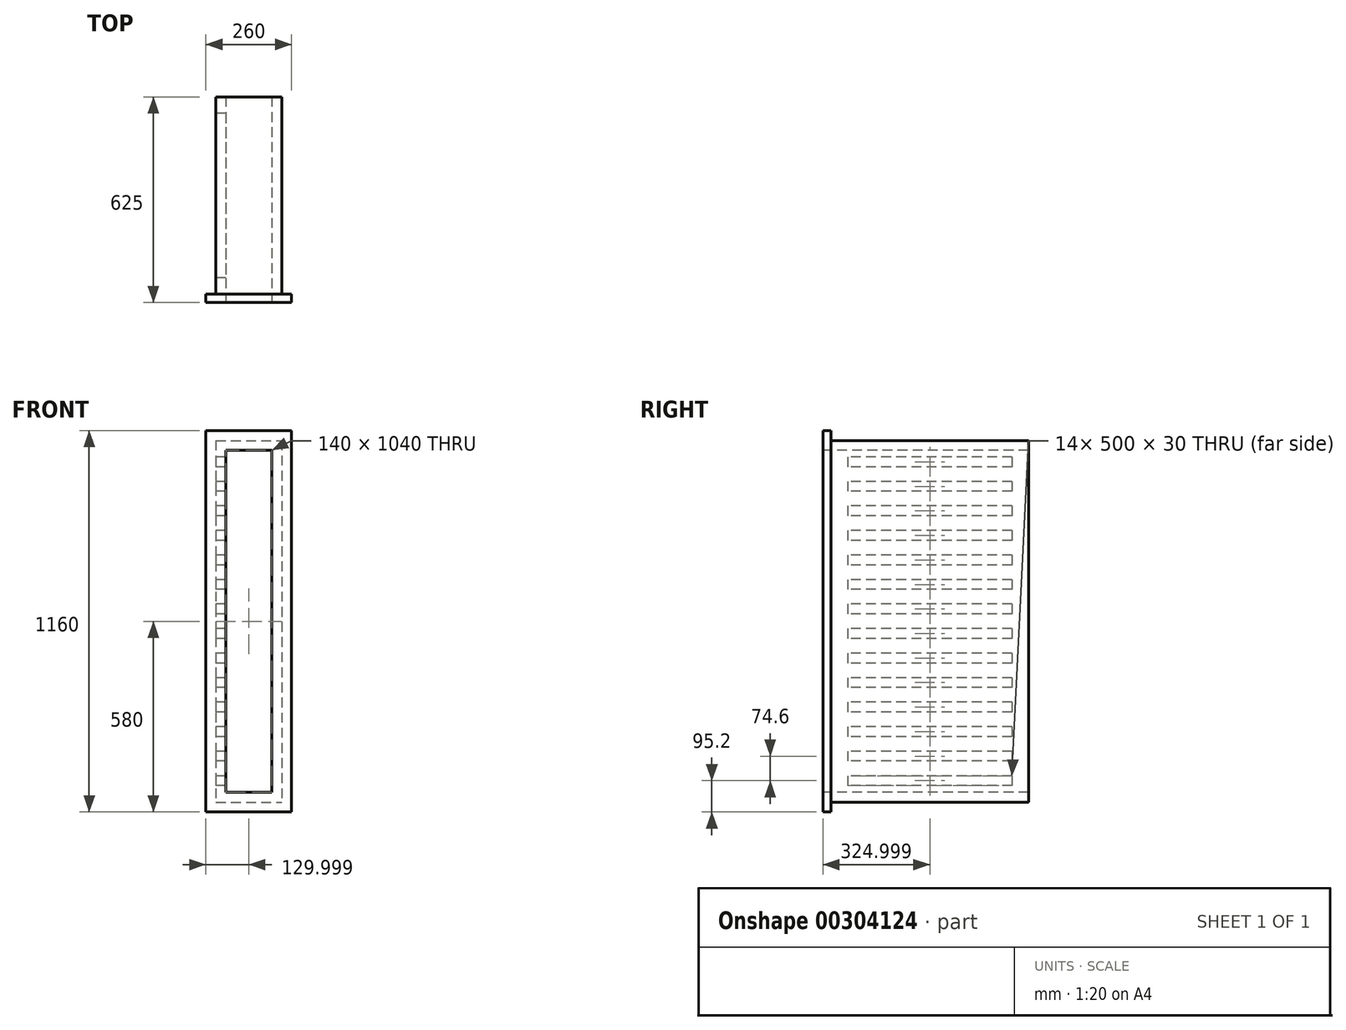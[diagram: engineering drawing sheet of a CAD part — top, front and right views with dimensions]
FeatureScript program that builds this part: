
annotation { "Feature Type Name" : "Feature", "Feature Type Description" : "" }
export const myFeature = defineFeature(function(context is Context, id is Id, definition is map)
    precondition{}
    {
        {
            var Q0;
            Q0=qCreatedBy(makeId("Top.planeOp"),FACE);
            var sketch = newSketch(context, id + "F0", { "sketchPlane" : qUnion([Q0])});
            skLineSegment(sketch, "E0.bottom", {"start": v(-110.21, 294.83) * mm, "end": v(89.79, 294.83) * mm});
            skLineSegment(sketch, "E0.top", {"start": v(-110.21, -305.17) * mm, "end": v(89.79, -305.17) * mm});
            skLineSegment(sketch, "E0.left", {"start": v(-110.21, 294.83) * mm, "end": v(-110.21, -305.17) * mm});
            skLineSegment(sketch, "E0.right", {"start": v(89.79, 294.83) * mm, "end": v(89.79, -305.17) * mm});
            skSolve(sketch);
        }
        {
            var Q0;
            Q0=makeQuery(id+"F0.imprint","IMPRINT",FACE,{"disambiguationData":[TD([[makeQuery(id+"F0.imprint","IMPRINT",EDGE,{"derivedFrom":sQuery(id+"F0.wireOp",EDGE,"E0.bottom")}),-1.0]])]});
            extrude(context, id + "F1", {"entities" : qUnion([Q0]), "depth" : 1100 * mm, "offsetDistance" : 25 * mm});
        }
        {
            var Q0;
            Q0=makeQuery(id+"F1.opExtrude","SWEPT_FACE",FACE,{"disambiguationData":[OSD([sQuery(id+"F0.wireOp",EDGE,"E0.top")])]});
            var sketch = newSketch(context, id + "F2", { "sketchPlane" : qUnion([Q0])});
            skLineSegment(sketch, "E1.bottom", {"start": v(59.79, 1070) * mm, "end": v(-80.21, 1070) * mm});
            skLineSegment(sketch, "E1.top", {"start": v(59.79, 30) * mm, "end": v(-80.21, 30) * mm});
            skLineSegment(sketch, "E1.left", {"start": v(59.79, 1070) * mm, "end": v(59.79, 30) * mm});
            skLineSegment(sketch, "E1.right", {"start": v(-80.21, 1070) * mm, "end": v(-80.21, 30) * mm});
            skSolve(sketch);
        }
        {
            var Q0;
            Q0=makeQuery(id+"F2.imprint","IMPRINT",FACE,{"disambiguationData":[TD([[makeQuery(id+"F2.imprint","IMPRINT",EDGE,{"derivedFrom":sQuery(id+"F2.wireOp",EDGE,"E1.bottom")}),1.0]])]});
            extrude(context, id + "F3", {"entities" : qUnion([Q0]), "operationType" : NewBodyOperationType.REMOVE, "endBound" : BoundingType.UP_TO_NEXT, "oppositeDirection" : true, "depth" : 25 * mm, "offsetDistance" : 25 * mm});
        }
        {
            var Q0;
            Q0=makeQuery(id+"F1.opExtrude","SWEPT_FACE",FACE,{"disambiguationData":[OSD([sQuery(id+"F0.wireOp",EDGE,"E0.left")])]});
            var sketch = newSketch(context, id + "F4", { "sketchPlane" : qUnion([Q0])});
            skLineSegment(sketch, "E2.bottom", {"start": v(-244.83, 1050) * mm, "end": v(255.17, 1050) * mm});
            skLineSegment(sketch, "E2.top", {"start": v(-244.83, 1020) * mm, "end": v(255.17, 1020) * mm});
            skLineSegment(sketch, "E2.left", {"start": v(-244.83, 1050) * mm, "end": v(-244.83, 1020) * mm});
            skLineSegment(sketch, "E2.right", {"start": v(255.17, 1050) * mm, "end": v(255.17, 1020) * mm});
            skLineSegment(sketch, "E3.bottom", {"start": v(-244.83, 900.8) * mm, "end": v(255.17, 900.8) * mm});
            skLineSegment(sketch, "E3.top", {"start": v(-244.83, 870.8) * mm, "end": v(255.17, 870.8) * mm});
            skLineSegment(sketch, "E3.left", {"start": v(-244.83, 900.8) * mm, "end": v(-244.83, 870.8) * mm});
            skLineSegment(sketch, "E3.right", {"start": v(255.17, 900.8) * mm, "end": v(255.17, 870.8) * mm});
            skLineSegment(sketch, "E4.bottom", {"start": v(-244.83, 751.6) * mm, "end": v(255.17, 751.6) * mm});
            skLineSegment(sketch, "E4.top", {"start": v(-244.83, 721.6) * mm, "end": v(255.17, 721.6) * mm});
            skLineSegment(sketch, "E4.left", {"start": v(-244.83, 751.6) * mm, "end": v(-244.83, 721.6) * mm});
            skLineSegment(sketch, "E4.right", {"start": v(255.17, 751.6) * mm, "end": v(255.17, 721.6) * mm});
            skLineSegment(sketch, "E5.bottom", {"start": v(-244.83, 677) * mm, "end": v(255.17, 677) * mm});
            skLineSegment(sketch, "E5.top", {"start": v(-244.83, 647) * mm, "end": v(255.17, 647) * mm});
            skLineSegment(sketch, "E5.left", {"start": v(-244.83, 677) * mm, "end": v(-244.83, 647) * mm});
            skLineSegment(sketch, "E5.right", {"start": v(255.17, 677) * mm, "end": v(255.17, 647) * mm});
            skLineSegment(sketch, "E6.bottom", {"start": v(-244.83, 602.4) * mm, "end": v(255.17, 602.4) * mm});
            skLineSegment(sketch, "E6.top", {"start": v(-244.83, 572.4) * mm, "end": v(255.17, 572.4) * mm});
            skLineSegment(sketch, "E6.left", {"start": v(-244.83, 602.4) * mm, "end": v(-244.83, 572.4) * mm});
            skLineSegment(sketch, "E6.right", {"start": v(255.17, 602.4) * mm, "end": v(255.17, 572.4) * mm});
            skLineSegment(sketch, "E7.bottom", {"start": v(-244.83, 527.8) * mm, "end": v(255.17, 527.8) * mm});
            skLineSegment(sketch, "E7.top", {"start": v(-244.83, 497.8) * mm, "end": v(255.17, 497.8) * mm});
            skLineSegment(sketch, "E7.left", {"start": v(-244.83, 527.8) * mm, "end": v(-244.83, 497.8) * mm});
            skLineSegment(sketch, "E7.right", {"start": v(255.17, 527.8) * mm, "end": v(255.17, 497.8) * mm});
            skLineSegment(sketch, "E8.bottom", {"start": v(-244.83, 453.2) * mm, "end": v(255.17, 453.2) * mm});
            skLineSegment(sketch, "E8.top", {"start": v(-244.83, 423.2) * mm, "end": v(255.17, 423.2) * mm});
            skLineSegment(sketch, "E8.left", {"start": v(-244.83, 453.2) * mm, "end": v(-244.83, 423.2) * mm});
            skLineSegment(sketch, "E8.right", {"start": v(255.17, 453.2) * mm, "end": v(255.17, 423.2) * mm});
            skLineSegment(sketch, "E9.bottom", {"start": v(-244.83, 378.6) * mm, "end": v(255.17, 378.6) * mm});
            skLineSegment(sketch, "E9.top", {"start": v(-244.83, 348.6) * mm, "end": v(255.17, 348.6) * mm});
            skLineSegment(sketch, "E9.left", {"start": v(-244.83, 378.6) * mm, "end": v(-244.83, 348.6) * mm});
            skLineSegment(sketch, "E9.right", {"start": v(255.17, 378.6) * mm, "end": v(255.17, 348.6) * mm});
            skLineSegment(sketch, "E10.bottom", {"start": v(-244.83, 304) * mm, "end": v(255.17, 304) * mm});
            skLineSegment(sketch, "E10.top", {"start": v(-244.83, 274) * mm, "end": v(255.17, 274) * mm});
            skLineSegment(sketch, "E10.left", {"start": v(-244.83, 304) * mm, "end": v(-244.83, 274) * mm});
            skLineSegment(sketch, "E10.right", {"start": v(255.17, 304) * mm, "end": v(255.17, 274) * mm});
            skLineSegment(sketch, "E11.bottom", {"start": v(-244.83, 229.4) * mm, "end": v(255.17, 229.4) * mm});
            skLineSegment(sketch, "E11.top", {"start": v(-244.83, 199.4) * mm, "end": v(255.17, 199.4) * mm});
            skLineSegment(sketch, "E11.left", {"start": v(-244.83, 229.4) * mm, "end": v(-244.83, 199.4) * mm});
            skLineSegment(sketch, "E11.right", {"start": v(255.17, 229.4) * mm, "end": v(255.17, 199.4) * mm});
            skLineSegment(sketch, "E12.bottom", {"start": v(-244.83, 154.8) * mm, "end": v(255.17, 154.8) * mm});
            skLineSegment(sketch, "E12.top", {"start": v(-244.83, 124.8) * mm, "end": v(255.17, 124.8) * mm});
            skLineSegment(sketch, "E12.left", {"start": v(-244.83, 154.8) * mm, "end": v(-244.83, 124.8) * mm});
            skLineSegment(sketch, "E12.right", {"start": v(255.17, 154.8) * mm, "end": v(255.17, 124.8) * mm});
            skLineSegment(sketch, "E13.bottom", {"start": v(-244.83, 80.2) * mm, "end": v(255.17, 80.2) * mm});
            skLineSegment(sketch, "E13.top", {"start": v(-244.83, 50.2) * mm, "end": v(255.17, 50.2) * mm});
            skLineSegment(sketch, "E13.left", {"start": v(-244.83, 80.2) * mm, "end": v(-244.83, 50.2) * mm});
            skLineSegment(sketch, "E13.right", {"start": v(255.17, 80.2) * mm, "end": v(255.17, 50.2) * mm});
            skLineSegment(sketch, "E14.bottom", {"start": v(-244.83, 826.2) * mm, "end": v(255.17, 826.2) * mm});
            skLineSegment(sketch, "E14.top", {"start": v(-244.83, 796.2) * mm, "end": v(255.17, 796.2) * mm});
            skLineSegment(sketch, "E14.left", {"start": v(-244.83, 826.2) * mm, "end": v(-244.83, 796.2) * mm});
            skLineSegment(sketch, "E14.right", {"start": v(255.17, 826.2) * mm, "end": v(255.17, 796.2) * mm});
            skLineSegment(sketch, "E15.bottom", {"start": v(-244.83, 975.4) * mm, "end": v(255.17, 975.4) * mm});
            skLineSegment(sketch, "E15.top", {"start": v(-244.83, 945.4) * mm, "end": v(255.17, 945.4) * mm});
            skLineSegment(sketch, "E15.left", {"start": v(-244.83, 975.4) * mm, "end": v(-244.83, 945.4) * mm});
            skLineSegment(sketch, "E15.right", {"start": v(255.17, 975.4) * mm, "end": v(255.17, 945.4) * mm});
            skSolve(sketch);
        }
        {
            var Q0;
            Q0=makeQuery(id+"F4.imprint","IMPRINT",FACE,{"disambiguationData":[TD([[makeQuery(id+"F4.imprint","IMPRINT",EDGE,{"derivedFrom":sQuery(id+"F4.wireOp",EDGE,"E2.bottom")}),-1.0]])]});
            var Q1;
            Q1=makeQuery(id+"F4.imprint","IMPRINT",FACE,{"disambiguationData":[TD([[makeQuery(id+"F4.imprint","IMPRINT",EDGE,{"derivedFrom":sQuery(id+"F4.wireOp",EDGE,"E15.bottom")}),-1.0]])]});
            var Q2;
            Q2=makeQuery(id+"F4.imprint","IMPRINT",FACE,{"disambiguationData":[TD([[makeQuery(id+"F4.imprint","IMPRINT",EDGE,{"derivedFrom":sQuery(id+"F4.wireOp",EDGE,"E3.bottom")}),-1.0]])]});
            var Q3;
            Q3=makeQuery(id+"F4.imprint","IMPRINT",FACE,{"disambiguationData":[TD([[makeQuery(id+"F4.imprint","IMPRINT",EDGE,{"derivedFrom":sQuery(id+"F4.wireOp",EDGE,"E14.bottom")}),-1.0]])]});
            var Q4;
            Q4=makeQuery(id+"F4.imprint","IMPRINT",FACE,{"disambiguationData":[TD([[makeQuery(id+"F4.imprint","IMPRINT",EDGE,{"derivedFrom":sQuery(id+"F4.wireOp",EDGE,"E4.bottom")}),-1.0]])]});
            var Q5;
            Q5=makeQuery(id+"F4.imprint","IMPRINT",FACE,{"disambiguationData":[TD([[makeQuery(id+"F4.imprint","IMPRINT",EDGE,{"derivedFrom":sQuery(id+"F4.wireOp",EDGE,"E5.bottom")}),-1.0]])]});
            var Q6;
            Q6=makeQuery(id+"F4.imprint","IMPRINT",FACE,{"disambiguationData":[TD([[makeQuery(id+"F4.imprint","IMPRINT",EDGE,{"derivedFrom":sQuery(id+"F4.wireOp",EDGE,"E6.bottom")}),-1.0]])]});
            var Q7;
            Q7=makeQuery(id+"F4.imprint","IMPRINT",FACE,{"disambiguationData":[TD([[makeQuery(id+"F4.imprint","IMPRINT",EDGE,{"derivedFrom":sQuery(id+"F4.wireOp",EDGE,"E7.bottom")}),-1.0]])]});
            var Q8;
            Q8=makeQuery(id+"F4.imprint","IMPRINT",FACE,{"disambiguationData":[TD([[makeQuery(id+"F4.imprint","IMPRINT",EDGE,{"derivedFrom":sQuery(id+"F4.wireOp",EDGE,"E8.bottom")}),-1.0]])]});
            var Q9;
            Q9=makeQuery(id+"F4.imprint","IMPRINT",FACE,{"disambiguationData":[TD([[makeQuery(id+"F4.imprint","IMPRINT",EDGE,{"derivedFrom":sQuery(id+"F4.wireOp",EDGE,"E9.bottom")}),-1.0]])]});
            var Q10;
            Q10=makeQuery(id+"F4.imprint","IMPRINT",FACE,{"disambiguationData":[TD([[makeQuery(id+"F4.imprint","IMPRINT",EDGE,{"derivedFrom":sQuery(id+"F4.wireOp",EDGE,"E10.bottom")}),-1.0]])]});
            var Q11;
            Q11=makeQuery(id+"F4.imprint","IMPRINT",FACE,{"disambiguationData":[TD([[makeQuery(id+"F4.imprint","IMPRINT",EDGE,{"derivedFrom":sQuery(id+"F4.wireOp",EDGE,"E11.bottom")}),-1.0]])]});
            var Q12;
            Q12=makeQuery(id+"F4.imprint","IMPRINT",FACE,{"disambiguationData":[TD([[makeQuery(id+"F4.imprint","IMPRINT",EDGE,{"derivedFrom":sQuery(id+"F4.wireOp",EDGE,"E12.bottom")}),-1.0]])]});
            var Q13;
            Q13=makeQuery(id+"F4.imprint","IMPRINT",FACE,{"disambiguationData":[TD([[makeQuery(id+"F4.imprint","IMPRINT",EDGE,{"derivedFrom":sQuery(id+"F4.wireOp",EDGE,"E13.bottom")}),-1.0]])]});
            extrude(context, id + "F5", {"entities" : qUnion([Q0, Q1, Q2, Q3, Q4, Q5, Q6, Q7, Q8, Q9, Q10, Q11, Q12, Q13]), "operationType" : NewBodyOperationType.REMOVE, "oppositeDirection" : true, "depth" : 30 * mm, "offsetDistance" : 25 * mm});
        }
        {
            var Q0;
            Q0=makeQuery(id+"F1.opExtrude","SWEPT_FACE",FACE,{"disambiguationData":[OSD([sQuery(id+"F0.wireOp",EDGE,"E0.top")])]});
            var sketch = newSketch(context, id + "F6", { "sketchPlane" : qUnion([Q0])});
            skLineSegment(sketch, "E16.bottom", {"start": v(-110.21, 1100) * mm, "end": v(89.79, 1100) * mm});
            skLineSegment(sketch, "E16.top", {"start": v(-110.21, 0) * mm, "end": v(89.79, 0) * mm});
            skLineSegment(sketch, "E16.left", {"start": v(-110.21, 1100) * mm, "end": v(-110.21, 0) * mm});
            skLineSegment(sketch, "E16.right", {"start": v(89.79, 1100) * mm, "end": v(89.79, 0) * mm});
            skLineSegment(sketch, "E17.0", {"start": v(-140.21, 1130) * mm, "end": v(119.79, 1130) * mm});
            skLineSegment(sketch, "E17.1", {"start": v(-140.21, 1130) * mm, "end": v(-140.21, -30) * mm});
            skLineSegment(sketch, "E17.2", {"start": v(-140.21, -30) * mm, "end": v(119.79, -30) * mm});
            skLineSegment(sketch, "E17.3", {"start": v(119.79, 1130) * mm, "end": v(119.79, -30) * mm});
            skSolve(sketch);
        }
        {
            var Q0;
            Q0=makeQuery(id+"F6.imprint","IMPRINT",FACE,{"disambiguationData":[TD([[makeQuery(id+"F6.imprint","IMPRINT",EDGE,{"derivedFrom":sQuery(id+"F6.wireOp",EDGE,"E16.bottom")}),1.0]])]});
            var Q1;
            Q1=makeQuery(id+"F6.imprint","IMPRINT",FACE,{"disambiguationData":[TD([[makeQuery(id+"F6.imprint","IMPRINT",EDGE,{"derivedFrom":sQuery(id+"F6.wireOp",EDGE,"E16.bottom")}),-1.0]])]});
            var Q2;
            Q2=makeQuery(id+"F6.imprint","IMPRINT",FACE,{"disambiguationData":[TD([[makeQuery(id+"F6.imprint","IMPRINT",EDGE,{"derivedFrom":makeQuery(id+"F3.boolean.opBoolean","COPY",EDGE,{"derivedFrom":makeQuery(id+"F3.opExtrude","CAP_EDGE",EDGE,{"disambiguationData":[OSD([sQuery(id+"F2.wireOp",EDGE,"E1.bottom")])],"isStart":true})})}),1.0]])]});
            extrude(context, id + "F7", {"entities" : qUnion([Q0, Q1, Q2]), "operationType" : NewBodyOperationType.ADD, "depth" : 25 * mm, "offsetDistance" : 25 * mm});
        }
    });
